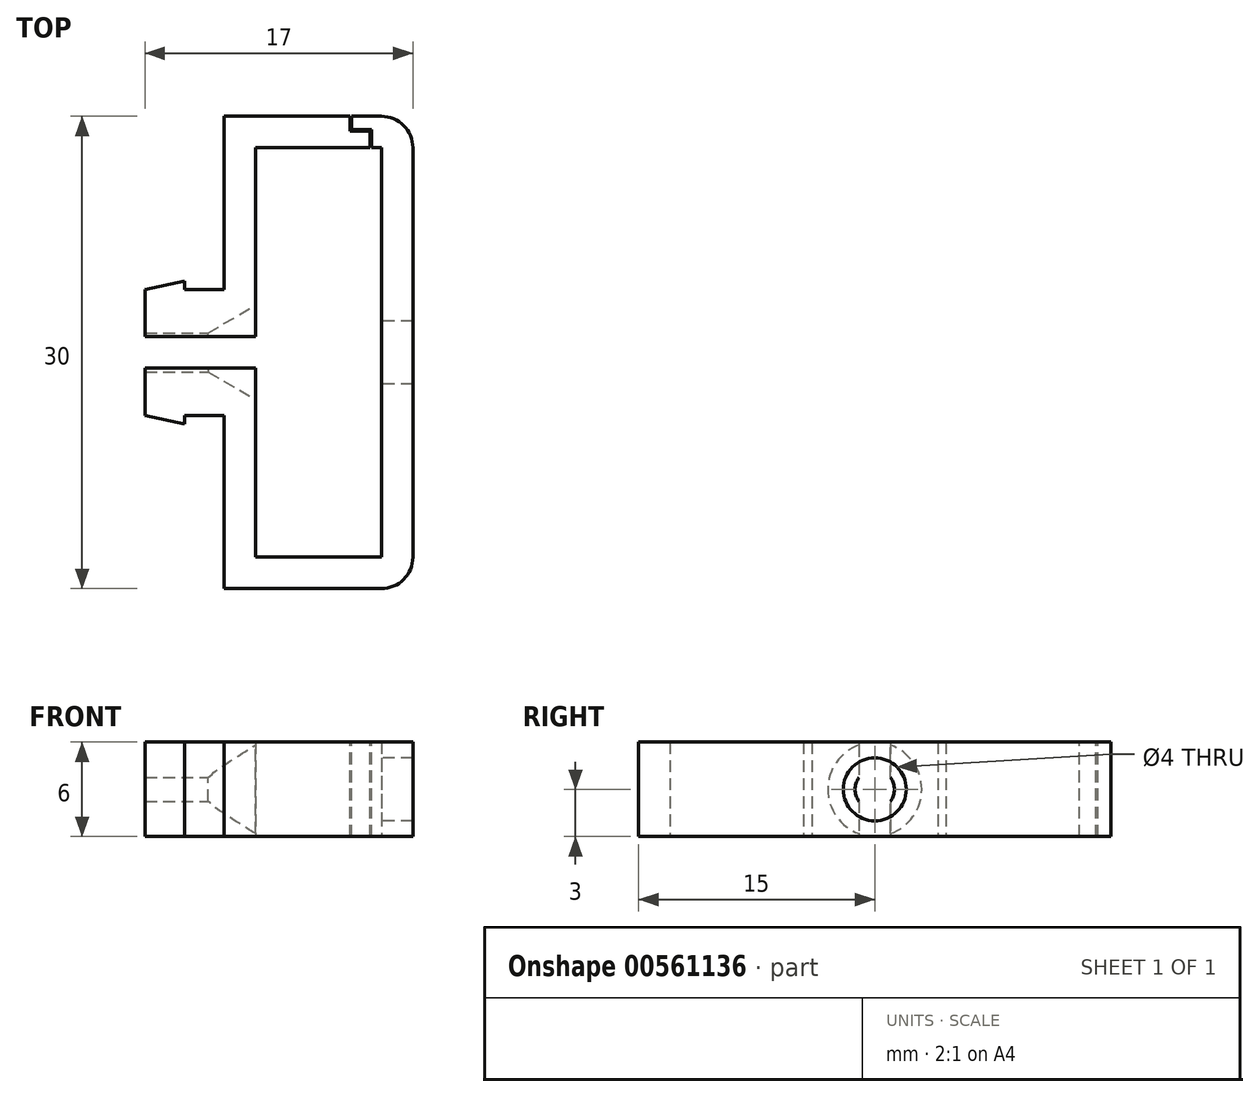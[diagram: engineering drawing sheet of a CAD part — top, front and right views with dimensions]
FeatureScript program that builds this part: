
annotation { "Feature Type Name" : "Feature", "Feature Type Description" : "" }
export const myFeature = defineFeature(function(context is Context, id is Id, definition is map)
    precondition{}
    {
        {
            var Q0;
            Q0=qCreatedBy(makeId("Top.planeOp"),FACE);
            var sketch = newSketch(context, id + "F0", { "sketchPlane" : qUnion([Q0])});
            skLineSegment(sketch, "E0.top", {"start": v(2.5, 8) * mm, "end": v(5, 8) * mm});
            skLineSegment(sketch, "E0.left", {"start": v(0, 5) * mm, "end": v(0, 8) * mm});
            skLineSegment(sketch, "E1", {"start": v(5, 4) * mm, "end": v(-16.31, 4) * mm, "construction": true});
            skLineSegment(sketch, "E2", {"start": v(5, 8) * mm, "end": v(5, 19) * mm});
            skLineSegment(sketch, "E3", {"start": v(5, 19) * mm, "end": v(6.96, 19) * mm});
            skLineSegment(sketch, "E4", {"start": v(6.96, 19) * mm, "end": v(17, 19) * mm});
            skLineSegment(sketch, "E5", {"start": v(17, 19) * mm, "end": v(17, 4) * mm});
            skLineSegment(sketch, "E6", {"start": v(15, 4) * mm, "end": v(15, 17) * mm});
            skLineSegment(sketch, "E7", {"start": v(15, 17) * mm, "end": v(7, 17) * mm});
            skLineSegment(sketch, "E8", {"start": v(7, 17) * mm, "end": v(7, 5) * mm});
            skLineSegment(sketch, "E9", {"start": v(2.5, 8) * mm, "end": v(2.5, 8.53) * mm});
            skLineSegment(sketch, "E10", {"start": v(2.5, 8.53) * mm, "end": v(0, 8) * mm});
            skPoint(sketch, "E0.bottom.end.orphan", {"position": v(5, 0) * mm});
            skLineSegment(sketch, "E11", {"start": v(5, 5) * mm, "end": v(0, 5) * mm});
            skLineSegment(sketch, "E12.MirrorCS", {"start": v(2.5, 0) * mm, "end": v(2.5, -0.53) * mm});
            skLineSegment(sketch, "E13.MirrorCS", {"start": v(0, 3) * mm, "end": v(0, 0) * mm});
            skLineSegment(sketch, "E14.MirrorCS", {"start": v(2.5, 0) * mm, "end": v(5, 0) * mm});
            skLineSegment(sketch, "E15.MirrorCS", {"start": v(5, 3) * mm, "end": v(0, 3) * mm});
            skLineSegment(sketch, "E16.MirrorCS", {"start": v(5, 0) * mm, "end": v(5, -11) * mm});
            skLineSegment(sketch, "E17.MirrorCS", {"start": v(5, -11) * mm, "end": v(6.96, -11) * mm});
            skLineSegment(sketch, "E18.MirrorCS", {"start": v(2.5, -0.53) * mm, "end": v(0, 0) * mm});
            skLineSegment(sketch, "E19.MirrorCS", {"start": v(6.96, -11) * mm, "end": v(17, -11) * mm});
            skLineSegment(sketch, "E20.MirrorCS", {"start": v(7, -9) * mm, "end": v(7, 3) * mm});
            skLineSegment(sketch, "E21.MirrorCS", {"start": v(15, -9) * mm, "end": v(7, -9) * mm});
            skLineSegment(sketch, "E22.MirrorCS", {"start": v(15, 4) * mm, "end": v(15, -9) * mm});
            skLineSegment(sketch, "E23.MirrorCS", {"start": v(17, -11) * mm, "end": v(17, 4) * mm});
            skLineSegment(sketch, "E24", {"start": v(5, 5) * mm, "end": v(7, 5) * mm});
            skLineSegment(sketch, "E25", {"start": v(5, 3) * mm, "end": v(7, 3) * mm});
            skPoint(sketch, "E26.MirrorCS.start.orphan", {"position": v(5, 4) * mm});
            skPoint(sketch, "E27.orphan", {"position": v(7, 4) * mm});
            skPoint(sketch, "E28.orphan", {"position": v(0, 4) * mm});
            skSolve(sketch);
        }
        {
            var Q0;
            Q0 = qSketchRegion(id + "F0", true);
            extrude(context, id + "F1", {"entities" : qUnion([Q0]), "depth" : 6 * mm, "offsetDistance" : 25 * mm});
        }
        {
            var Q0;
            Q0=makeQuery(id+"F1.opExtrude","SWEPT_FACE",FACE,{"disambiguationData":[OSD([sQuery(id+"F0.wireOp",EDGE,"E6"),sQuery(id+"F0.wireOp",EDGE,"E22.MirrorCS")])]});
            var sketch = newSketch(context, id + "F2", { "sketchPlane" : qUnion([Q0])});
            skCircle(sketch, "E29", {"center": v(-4, 3) * mm, "radius": 1.25 * mm});
            skPoint(sketch, "E29.centerSnap0", {"position": v(9, 3) * mm});
            skPoint(sketch, "E29.centerSnap1", {"position": v(-4, 6) * mm});
            skSolve(sketch);
        }
        {
            var Q0;
            Q0 = qSketchRegion(id + "F2", true);
            extrude(context, id + "F3", {"entities" : qUnion([Q0]), "operationType" : NewBodyOperationType.REMOVE, "depth" : 25 * mm, "offsetDistance" : 25 * mm});
        }
        {
            var Q0;
            Q0=makeQuery(id+"F1.opExtrude","SWEPT_FACE",FACE,{"disambiguationData":[OSD([sQuery(id+"F0.wireOp",EDGE,"E6"),sQuery(id+"F0.wireOp",EDGE,"E22.MirrorCS")])]});
            var sketch = newSketch(context, id + "F4", { "sketchPlane" : qUnion([Q0])});
            skCircle(sketch, "E30", {"center": v(-4, 3) * mm, "radius": 2 * mm});
            skPoint(sketch, "E30.centerSnap0", {"position": v(-17, 3) * mm});
            skPoint(sketch, "E30.centerSnap1", {"position": v(-4, 6) * mm});
            skSolve(sketch);
        }
        {
            var Q0;
            Q0 = qSketchRegion(id + "F4", true);
            extrude(context, id + "F5", {"entities" : qUnion([Q0]), "operationType" : NewBodyOperationType.REMOVE, "oppositeDirection" : true, "depth" : 25 * mm, "offsetDistance" : 25 * mm});
        }
        {
            var Q0;
            Q0=makeQuery(id+"F1.opExtrude","SWEPT_EDGE",EDGE,{"disambiguationData":[OSD([sQuery(id+"F0.wireOp",EDGE,"E4"),sQuery(id+"F0.wireOp",EDGE,"E5")])]});
            var Q1;
            Q1=makeQuery(id+"F1.opExtrude","SWEPT_EDGE",EDGE,{"disambiguationData":[OSD([sQuery(id+"F0.wireOp",EDGE,"E19.MirrorCS"),sQuery(id+"F0.wireOp",EDGE,"E23.MirrorCS")])]});
            fillet(context, id + "F6", {"entities" : qUnion([Q0, Q1]), "radius" : 2 * mm, "tangentPropagation" : true, "allowEdgeOverflow" : false});
        }
        {
            var Q0;
            Q0=makeQuery(id+"F3.boolean.opBoolean","INTERSECT",EDGE,{"derivedFrom":[makeQuery(id+"F1.opExtrude","SWEPT_FACE",FACE,{"disambiguationData":[OSD([sQuery(id+"F0.wireOp",EDGE,"E8")])]}),makeQuery(id+"F3.opExtrude","SWEPT_FACE",FACE,{"disambiguationData":[OSD([sQuery(id+"F2.wireOp",EDGE,"E29")])]})]});
            chamfer(context, id + "F7", {"entities" : qUnion([Q0]), "chamferType" : ChamferType.OFFSET_ANGLE, "width" : 3 * mm, "oppositeDirection" : true, "angle" : 30 * degree, "tangentPropagation" : true});
        }
        {
            var Q0;
            Q0=makeQuery(id+"F3.boolean.opBoolean","INTERSECT",EDGE,{"derivedFrom":[makeQuery(id+"F1.opExtrude","SWEPT_FACE",FACE,{"disambiguationData":[OSD([sQuery(id+"F0.wireOp",EDGE,"E20.MirrorCS")])]}),makeQuery(id+"F3.opExtrude","SWEPT_FACE",FACE,{"disambiguationData":[OSD([sQuery(id+"F2.wireOp",EDGE,"E29")])]})]});
            chamfer(context, id + "F8", {"entities" : qUnion([Q0]), "chamferType" : ChamferType.OFFSET_ANGLE, "width" : 3 * mm, "oppositeDirection" : false, "angle" : 30 * degree, "tangentPropagation" : true});
        }
        {
            var Q0;
            Q0=makeQuery(id+"F1.opExtrude","CAP_FACE",FACE,{"disambiguationData":[OSD([sQuery(id+"F0.wireOp",EDGE,"E0.top"),sQuery(id+"F0.wireOp",EDGE,"E0.left"),sQuery(id+"F0.wireOp",EDGE,"E2"),sQuery(id+"F0.wireOp",EDGE,"E3"),sQuery(id+"F0.wireOp",EDGE,"E4"),sQuery(id+"F0.wireOp",EDGE,"E5"),sQuery(id+"F0.wireOp",EDGE,"E6"),sQuery(id+"F0.wireOp",EDGE,"E7"),sQuery(id+"F0.wireOp",EDGE,"E8"),sQuery(id+"F0.wireOp",EDGE,"E9"),sQuery(id+"F0.wireOp",EDGE,"E10"),sQuery(id+"F0.wireOp",EDGE,"E11"),sQuery(id+"F0.wireOp",EDGE,"E12.MirrorCS"),sQuery(id+"F0.wireOp",EDGE,"E13.MirrorCS"),sQuery(id+"F0.wireOp",EDGE,"E14.MirrorCS"),sQuery(id+"F0.wireOp",EDGE,"E15.MirrorCS"),sQuery(id+"F0.wireOp",EDGE,"E16.MirrorCS"),sQuery(id+"F0.wireOp",EDGE,"E17.MirrorCS"),sQuery(id+"F0.wireOp",EDGE,"E18.MirrorCS"),sQuery(id+"F0.wireOp",EDGE,"E19.MirrorCS"),sQuery(id+"F0.wireOp",EDGE,"E20.MirrorCS"),sQuery(id+"F0.wireOp",EDGE,"E21.MirrorCS"),sQuery(id+"F0.wireOp",EDGE,"E22.MirrorCS"),sQuery(id+"F0.wireOp",EDGE,"E23.MirrorCS"),sQuery(id+"F0.wireOp",EDGE,"E24"),sQuery(id+"F0.wireOp",EDGE,"E25")])],"isStart":false});
            var sketch = newSketch(context, id + "F9", { "sketchPlane" : qUnion([Q0])});
            skLineSegment(sketch, "E31", {"start": v(13, 19) * mm, "end": v(13, 18.06) * mm});
            skLineSegment(sketch, "E32", {"start": v(13, 18.06) * mm, "end": v(14.28, 18.06) * mm});
            skLineSegment(sketch, "E33", {"start": v(14.28, 18.06) * mm, "end": v(14.28, 17) * mm});
            skLineSegment(sketch, "E34", {"start": v(13.1, 19) * mm, "end": v(13.1, 18.16) * mm});
            skLineSegment(sketch, "E35", {"start": v(13.1, 18.16) * mm, "end": v(14.38, 18.16) * mm});
            skLineSegment(sketch, "E36", {"start": v(14.38, 18.16) * mm, "end": v(14.38, 17) * mm});
            skLineSegment(sketch, "E37", {"start": v(13, 19) * mm, "end": v(13.1, 19) * mm});
            skLineSegment(sketch, "E38", {"start": v(14.28, 17) * mm, "end": v(14.38, 17) * mm});
            skSolve(sketch);
        }
        {
            var Q0;
            Q0=makeQuery(id+"F9.imprint","IMPRINT",FACE,{"disambiguationData":[TD([[makeQuery(id+"F9.imprint","IMPRINT",EDGE,{"derivedFrom":sQuery(id+"F9.wireOp",EDGE,"E31")}),1.0]])]});
            extrude(context, id + "F10", {"entities" : qUnion([Q0]), "operationType" : NewBodyOperationType.REMOVE, "oppositeDirection" : true, "depth" : 25 * mm, "offsetDistance" : 25 * mm});
        }
    });
